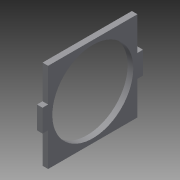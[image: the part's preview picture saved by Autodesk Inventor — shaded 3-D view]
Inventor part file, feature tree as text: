
AUTODESK INVENTOR PART (.ipt)
format: ipt  version: 2013 (Build 170138000, 138)  size: 93,184 bytes
history: native  units: in
note: dims shown in document units (in); Inventor stores cm internally (conversion verified against a paired STEP export)
features: extrude x1, sketch x1
ambient origin geometry x8: Origin, YZ Plane, XZ Plane, XY Plane, X Axis, Y Axis, Z Axis, Center Point
bodies: Solid1 (feature_tree)
feature tree (2):
  extrude  "Extrusion1"  Depth=2.0in
  sketch  "Sketch1"  dims[d0=3.622in d1=2.0in d2=2.0in d3=2.0in d4=1.5in d5=0.25in d6=1.0in d7=1.5in d8=4.0in d9=1.5in d10=0.25in d11=1.0in d12=0.25in d13=0.25in d14=0.0in]
